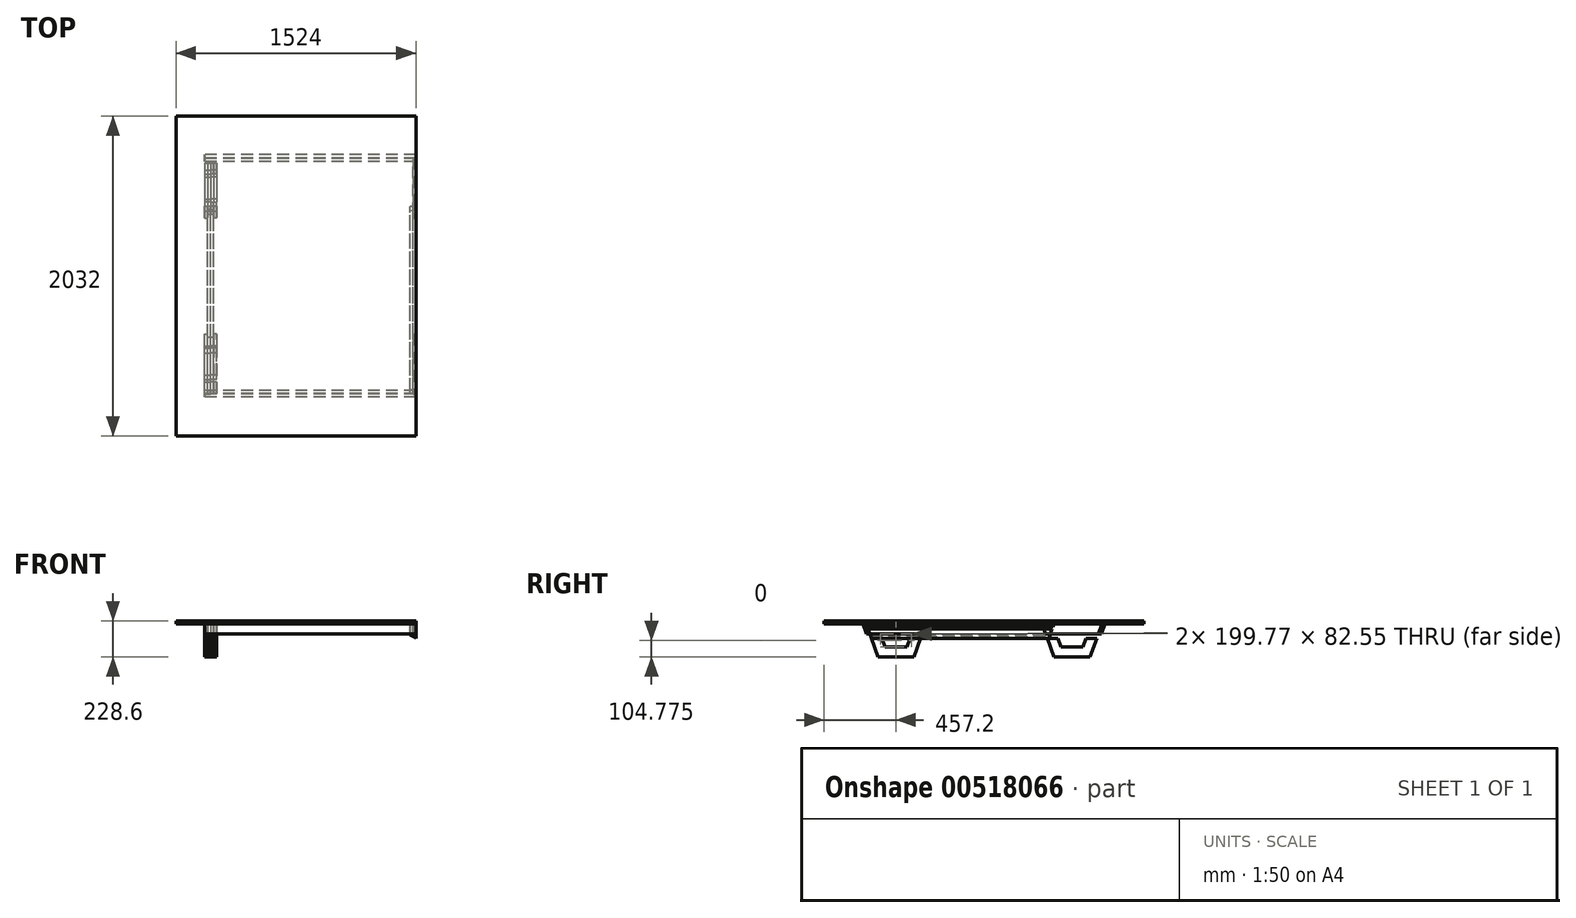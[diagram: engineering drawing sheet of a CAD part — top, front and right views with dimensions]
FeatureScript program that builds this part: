
annotation { "Feature Type Name" : "Feature", "Feature Type Description" : "" }
export const myFeature = defineFeature(function(context is Context, id is Id, definition is map)
    precondition{}
    {
        {
            var Q0;
            Q0=qCreatedBy(makeId("Top.planeOp"),FACE);
            var sketch = newSketch(context, id + "F0", { "sketchPlane" : qUnion([Q0])});
            skLineSegment(sketch, "E0.bottom", {"start": v(0, 0) * mm, "end": v(-1524, 0) * mm});
            skLineSegment(sketch, "E0.top", {"start": v(0, -2032) * mm, "end": v(-1524, -2032) * mm});
            skLineSegment(sketch, "E0.left", {"start": v(0, 0) * mm, "end": v(0, -2032) * mm});
            skLineSegment(sketch, "E0.right", {"start": v(-1524, 0) * mm, "end": v(-1524, -2032) * mm});
            skSolve(sketch);
        }
        {
            var Q0;
            Q0 = qSketchRegion(id + "F0", true);
            extrude(context, id + "F1", {"entities" : qUnion([Q0]), "depth" : 19.05 * mm, "offsetDistance" : 25.4 * mm});
        }
        {
            var Q0;
            Q0=qCreatedBy(makeId("Front.planeOp"),FACE);
            var sketch = newSketch(context, id + "F2", { "sketchPlane" : qUnion([Q0])});
            skLineSegment(sketch, "E1.bottom", {"start": v(0, -31.75) * mm, "end": v(-19.05, -31.75) * mm});
            skLineSegment(sketch, "E1.top", {"start": v(0, -69.85) * mm, "end": v(-19.05, -69.85) * mm, "construction": true});
            skLineSegment(sketch, "E1.left", {"start": v(0, -31.75) * mm, "end": v(0, -69.85) * mm});
            skLineSegment(sketch, "E1.right", {"start": v(-19.05, -31.75) * mm, "end": v(-19.05, -69.85) * mm});
            skLineSegment(sketch, "E2.bottom", {"start": v(-19.05, -69.85) * mm, "end": v(-38.1, -69.85) * mm, "construction": true});
            skLineSegment(sketch, "E2.top", {"start": v(-19.05, -6.35) * mm, "end": v(-38.1, -6.35) * mm});
            skLineSegment(sketch, "E2.left", {"start": v(-19.05, -69.85) * mm, "end": v(-19.05, -6.35) * mm});
            skLineSegment(sketch, "E2.right", {"start": v(-38.1, -69.85) * mm, "end": v(-38.1, -6.35) * mm});
            skLineSegment(sketch, "E3", {"start": v(-38.1, -69.85) * mm, "end": v(0, -91.85) * mm});
            skLineSegment(sketch, "E4", {"start": v(0, -91.85) * mm, "end": v(0, -69.85) * mm});
            skLineSegment(sketch, "E5", {"start": v(-19.05, -69.85) * mm, "end": v(-19.05, -80.85) * mm});
            skLineSegment(sketch, "E6", {"start": v(0, -91.85) * mm, "end": v(-123.42, -91.85) * mm, "construction": true});
            skSolve(sketch);
        }
        {
            var Q0;
            {var subQ0=sQuery(id+"F2.wireOp",EDGE,"E1.bottom");Q0=makeQuery(id+"F2.imprint","IMPRINT",FACE,{"disambiguationData":[TD([[makeQuery(id+"F2.imprint","IMPRINT",EDGE,{"derivedFrom":subQ0}),1.0]])]});}
            var Q1;
            Q1=makeQuery(id+"F1.opExtrude","SWEPT_FACE",FACE,{"disambiguationData":[OSD([sQuery(id+"F0.wireOp",EDGE,"E0.top")])]});
            extrude(context, id + "F3", {"entities" : qUnion([Q0]), "endBound" : BoundingType.UP_TO_SURFACE, "depth" : 25.4 * mm, "endBoundEntityFace" : qUnion([Q1]), "offsetDistance" : 25.4 * mm});
        }
        {
            var Q0;
            {var subQ3=sQuery(id+"F2.wireOp",EDGE,"E2.top");Q0=makeQuery(id+"F2.imprint","IMPRINT",FACE,{"disambiguationData":[TD([[makeQuery(id+"F2.imprint","IMPRINT",EDGE,{"derivedFrom":subQ3}),1.0]])]});}
            var Q1;
            Q1=makeQuery(id+"F3.opExtrude","CAP_FACE",FACE,{"disambiguationData":[OSD([sQuery(id+"F2.wireOp",EDGE,"E1.bottom"),sQuery(id+"F2.wireOp",EDGE,"E1.left"),sQuery(id+"F2.wireOp",EDGE,"E2.left"),sQuery(id+"F2.wireOp",EDGE,"E3"),sQuery(id+"F2.wireOp",EDGE,"E4"),sQuery(id+"F2.wireOp",EDGE,"E5")])],"isStart":false});
            extrude(context, id + "F4", {"entities" : qUnion([Q0]), "endBound" : BoundingType.UP_TO_SURFACE, "depth" : 25.4 * mm, "endBoundEntityFace" : qUnion([Q1]), "offsetDistance" : 25.4 * mm});
        }
        {
            var Q0;
            Q0=qCreatedBy(makeId("Front.planeOp"),FACE);
            var sketch = newSketch(context, id + "F5", { "sketchPlane" : qUnion([Q0])});
            skLineSegment(sketch, "E7.bottom", {"start": v(0, 0) * mm, "end": v(-19.05, 0) * mm});
            skLineSegment(sketch, "E7.top", {"start": v(0, -19.05) * mm, "end": v(-19.05, -19.05) * mm});
            skLineSegment(sketch, "E7.left", {"start": v(0, 0) * mm, "end": v(0, -19.05) * mm});
            skLineSegment(sketch, "E7.right", {"start": v(-19.05, 0) * mm, "end": v(-19.05, -19.05) * mm});
            skSolve(sketch);
        }
        {
            var Q0;
            Q0 = qSketchRegion(id + "F5", true);
            var Q1;
            Q1=makeQuery(id+"F1.opExtrude","SWEPT_FACE",FACE,{"disambiguationData":[OSD([sQuery(id+"F0.wireOp",EDGE,"E0.top")])]});
            extrude(context, id + "F6", {"entities" : qUnion([Q0]), "endBound" : BoundingType.UP_TO_SURFACE, "depth" : 25.4 * mm, "endBoundEntityFace" : qUnion([Q1]), "offsetDistance" : 25.4 * mm});
        }
        {
            var Q0;
            Q0=qCreatedBy(makeId("Front.planeOp"),FACE);
            var sketch = newSketch(context, id + "F7", { "sketchPlane" : qUnion([Q0])});
            skLineSegment(sketch, "E8.bottom", {"start": v(-1304.93, 0) * mm, "end": v(-1285.88, 0) * mm});
            skLineSegment(sketch, "E8.top", {"start": v(-1304.93, -63.5) * mm, "end": v(-1285.88, -63.5) * mm});
            skLineSegment(sketch, "E8.left", {"start": v(-1304.93, 0) * mm, "end": v(-1304.93, -63.5) * mm});
            skLineSegment(sketch, "E8.right", {"start": v(-1285.88, 0) * mm, "end": v(-1285.88, -63.5) * mm});
            skPoint(sketch, "E9", {"position": v(-1295.4, 0) * mm});
            skSolve(sketch);
        }
        {
            var Q0;
            Q0 = qSketchRegion(id + "F7", true);
            var Q1;
            Q1=makeQuery(id+"F1.opExtrude","SWEPT_FACE",FACE,{"disambiguationData":[OSD([sQuery(id+"F0.wireOp",EDGE,"E0.top")])]});
            extrude(context, id + "F8", {"entities" : qUnion([Q0]), "endBound" : BoundingType.UP_TO_SURFACE, "depth" : 25.4 * mm, "endBoundEntityFace" : qUnion([Q1]), "offsetDistance" : 25.4 * mm});
        }
        {
            var Q0;
            Q0=makeQuery(id+"F8.opExtrude","SWEPT_FACE",FACE,{"disambiguationData":[OSD([sQuery(id+"F7.wireOp",EDGE,"E8.left")])]});
            var sketch = newSketch(context, id + "F9", { "sketchPlane" : qUnion([Q0])});
            skLineSegment(sketch, "E10", {"start": v(1765.37, 0) * mm, "end": v(1689.1, -209.55) * mm});
            skLineSegment(sketch, "E11", {"start": v(1689.1, -209.55) * mm, "end": v(1460.5, -209.55) * mm});
            skLineSegment(sketch, "E12", {"start": v(1460.5, -209.55) * mm, "end": v(1384.23, 0) * mm});
            skLineSegment(sketch, "E13", {"start": v(1384.23, 0) * mm, "end": v(1765.37, 0) * mm});
            skLineSegment(sketch, "E14.0", {"start": v(1474.92, -63.5) * mm, "end": v(1674.68, -63.5) * mm});
            skLineSegment(sketch, "E14.1", {"start": v(1504.96, -146.05) * mm, "end": v(1474.92, -63.5) * mm});
            skLineSegment(sketch, "E14.2", {"start": v(1644.64, -146.05) * mm, "end": v(1504.96, -146.05) * mm});
            skLineSegment(sketch, "E14.3", {"start": v(1674.68, -63.5) * mm, "end": v(1644.64, -146.05) * mm});
            skPoint(sketch, "E15", {"position": v(1574.8, 0) * mm});
            skLineSegment(sketch, "E16", {"start": v(1016, 0) * mm, "end": v(1016, -260.73) * mm, "construction": true});
            skPoint(sketch, "E17.MirrorP", {"position": v(457.2, 0) * mm});
            skLineSegment(sketch, "E18.MirrorCS", {"start": v(357.32, -63.5) * mm, "end": v(387.36, -146.05) * mm});
            skLineSegment(sketch, "E19.MirrorCS", {"start": v(387.36, -146.05) * mm, "end": v(527.04, -146.05) * mm});
            skLineSegment(sketch, "E20.MirrorCS", {"start": v(527.04, -146.05) * mm, "end": v(557.08, -63.5) * mm});
            skLineSegment(sketch, "E21.MirrorCS", {"start": v(557.08, -63.5) * mm, "end": v(357.32, -63.5) * mm});
            skLineSegment(sketch, "E22.MirrorCS", {"start": v(266.63, 0) * mm, "end": v(342.9, -209.55) * mm});
            skLineSegment(sketch, "E23.MirrorCS", {"start": v(647.77, 0) * mm, "end": v(266.63, 0) * mm});
            skLineSegment(sketch, "E24.MirrorCS", {"start": v(342.9, -209.55) * mm, "end": v(571.5, -209.55) * mm});
            skLineSegment(sketch, "E25.MirrorCS", {"start": v(571.5, -209.55) * mm, "end": v(647.77, 0) * mm});
            skSolve(sketch);
        }
        {
            var Q0;
            Q0 = qSketchRegion(id + "F9", true);
            extrude(context, id + "F10", {"entities" : qUnion([Q0]), "depth" : 19.05 * mm, "offsetDistance" : 25.4 * mm});
        }
        {
            var Q0;
            Q0=makeQuery(id+"F10.opExtrude","CAP_FACE",FACE,{"disambiguationData":[OSD([sQuery(id+"F9.wireOp",EDGE,"E10"),sQuery(id+"F9.wireOp",EDGE,"E11"),sQuery(id+"F9.wireOp",EDGE,"E12"),sQuery(id+"F9.wireOp",EDGE,"E13"),sQuery(id+"F9.wireOp",EDGE,"E14.0"),sQuery(id+"F9.wireOp",EDGE,"E14.1"),sQuery(id+"F9.wireOp",EDGE,"E14.2"),sQuery(id+"F9.wireOp",EDGE,"E14.3")])],"isStart":true});
            var Q1;
            Q1=makeQuery(id+"F10.opExtrude","CAP_FACE",FACE,{"disambiguationData":[OSD([sQuery(id+"F9.wireOp",EDGE,"E18.MirrorCS"),sQuery(id+"F9.wireOp",EDGE,"E19.MirrorCS"),sQuery(id+"F9.wireOp",EDGE,"E20.MirrorCS"),sQuery(id+"F9.wireOp",EDGE,"E21.MirrorCS"),sQuery(id+"F9.wireOp",EDGE,"E22.MirrorCS"),sQuery(id+"F9.wireOp",EDGE,"E23.MirrorCS"),sQuery(id+"F9.wireOp",EDGE,"E24.MirrorCS"),sQuery(id+"F9.wireOp",EDGE,"E25.MirrorCS")])],"isStart":true});
            extrude(context, id + "F11", {"entities" : qUnion([Q0, Q1]), "depth" : 19.05 * mm, "offsetDistance" : 25.4 * mm});
        }
        {
            var Q0;
            Q0=makeQuery(id+"F8.opExtrude","SWEPT_BODY",BODY,{"disambiguationData":[OSD([sQuery(id+"F7.wireOp",EDGE,"E8.bottom"),sQuery(id+"F7.wireOp",EDGE,"E8.top"),sQuery(id+"F7.wireOp",EDGE,"E8.left"),sQuery(id+"F7.wireOp",EDGE,"E8.right")])]});
            var Q1;
            Q1=makeQuery(id+"F11.opExtrude","SWEPT_BODY",BODY,{"disambiguationData":[OSD([sQuery(id+"F9.wireOp",EDGE,"E10"),sQuery(id+"F9.wireOp",EDGE,"E11"),sQuery(id+"F9.wireOp",EDGE,"E12"),sQuery(id+"F9.wireOp",EDGE,"E13"),sQuery(id+"F9.wireOp",EDGE,"E14.0"),sQuery(id+"F9.wireOp",EDGE,"E14.1"),sQuery(id+"F9.wireOp",EDGE,"E14.2"),sQuery(id+"F9.wireOp",EDGE,"E14.3")])]});
            var Q2;
            Q2=makeQuery(id+"F11.opExtrude","SWEPT_BODY",BODY,{"disambiguationData":[OSD([sQuery(id+"F9.wireOp",EDGE,"E18.MirrorCS"),sQuery(id+"F9.wireOp",EDGE,"E19.MirrorCS"),sQuery(id+"F9.wireOp",EDGE,"E20.MirrorCS"),sQuery(id+"F9.wireOp",EDGE,"E21.MirrorCS"),sQuery(id+"F9.wireOp",EDGE,"E22.MirrorCS"),sQuery(id+"F9.wireOp",EDGE,"E23.MirrorCS"),sQuery(id+"F9.wireOp",EDGE,"E24.MirrorCS"),sQuery(id+"F9.wireOp",EDGE,"E25.MirrorCS")])]});
            booleanBodies(context, id + "F12", {"operationType" : BooleanOperationType.SUBTRACTION, "tools" : qUnion([Q0]), "targets" : qUnion([Q1, Q2]), "keepTools" : true});
        }
        {
            var Q0;
            Q0=makeQuery(id+"F8.opExtrude","SWEPT_FACE",FACE,{"disambiguationData":[OSD([sQuery(id+"F7.wireOp",EDGE,"E8.right")])]});
            var sketch = newSketch(context, id + "F13", { "sketchPlane" : qUnion([Q0])});
            skLineSegment(sketch, "E26.0.0", {"start": v(-1765.37, 0) * mm, "end": v(-1384.23, 0) * mm});
            skLineSegment(sketch, "E26.0.1", {"start": v(-1384.23, 0) * mm, "end": v(-1460.5, -209.55) * mm});
            skLineSegment(sketch, "E26.0.2", {"start": v(-1460.5, -209.55) * mm, "end": v(-1689.1, -209.55) * mm});
            skLineSegment(sketch, "E26.0.3", {"start": v(-1689.1, -209.55) * mm, "end": v(-1765.37, 0) * mm});
            skLineSegment(sketch, "E26.1.0", {"start": v(-342.9, -209.55) * mm, "end": v(-571.5, -209.55) * mm});
            skLineSegment(sketch, "E26.1.1", {"start": v(-571.5, -209.55) * mm, "end": v(-647.77, 0) * mm});
            skLineSegment(sketch, "E26.1.2", {"start": v(-647.77, 0) * mm, "end": v(-266.63, 0) * mm});
            skLineSegment(sketch, "E26.1.3", {"start": v(-266.63, 0) * mm, "end": v(-342.9, -209.55) * mm});
            skLineSegment(sketch, "E27.0", {"start": v(-1674.68, -63.5) * mm, "end": v(-1474.92, -63.5) * mm});
            skLineSegment(sketch, "E27.1", {"start": v(-1504.96, -146.05) * mm, "end": v(-1474.92, -63.5) * mm});
            skLineSegment(sketch, "E27.2", {"start": v(-1674.68, -63.5) * mm, "end": v(-1644.64, -146.05) * mm});
            skLineSegment(sketch, "E27.3", {"start": v(-1644.64, -146.05) * mm, "end": v(-1504.96, -146.05) * mm});
            skLineSegment(sketch, "E28.0", {"start": v(-557.08, -63.5) * mm, "end": v(-357.32, -63.5) * mm});
            skLineSegment(sketch, "E28.1", {"start": v(-357.32, -63.5) * mm, "end": v(-387.36, -146.05) * mm});
            skLineSegment(sketch, "E28.2", {"start": v(-527.04, -146.05) * mm, "end": v(-557.08, -63.5) * mm});
            skLineSegment(sketch, "E28.3", {"start": v(-387.36, -146.05) * mm, "end": v(-527.04, -146.05) * mm});
            skSolve(sketch);
        }
        {
            var Q0;
            Q0 = qSketchRegion(id + "F13", true);
            extrude(context, id + "F14", {"entities" : qUnion([Q0]), "depth" : 19.05 * mm, "offsetDistance" : 25.4 * mm});
        }
        {
            var Q0;
            Q0=makeQuery(id+"F10.opExtrude","CAP_FACE",FACE,{"disambiguationData":[OSD([sQuery(id+"F9.wireOp",EDGE,"E10"),sQuery(id+"F9.wireOp",EDGE,"E11"),sQuery(id+"F9.wireOp",EDGE,"E12"),sQuery(id+"F9.wireOp",EDGE,"E13"),sQuery(id+"F9.wireOp",EDGE,"E14.0"),sQuery(id+"F9.wireOp",EDGE,"E14.1"),sQuery(id+"F9.wireOp",EDGE,"E14.2"),sQuery(id+"F9.wireOp",EDGE,"E14.3")])],"isStart":false});
            var Q1;
            Q1=makeQuery(id+"F10.opExtrude","CAP_FACE",FACE,{"disambiguationData":[OSD([sQuery(id+"F9.wireOp",EDGE,"E18.MirrorCS"),sQuery(id+"F9.wireOp",EDGE,"E19.MirrorCS"),sQuery(id+"F9.wireOp",EDGE,"E20.MirrorCS"),sQuery(id+"F9.wireOp",EDGE,"E21.MirrorCS"),sQuery(id+"F9.wireOp",EDGE,"E22.MirrorCS"),sQuery(id+"F9.wireOp",EDGE,"E23.MirrorCS"),sQuery(id+"F9.wireOp",EDGE,"E24.MirrorCS"),sQuery(id+"F9.wireOp",EDGE,"E25.MirrorCS")])],"isStart":false});
            extrude(context, id + "F15", {"entities" : qUnion([Q0, Q1]), "depth" : 19.05 * mm, "offsetDistance" : 25.4 * mm});
        }
        {
            var Q0;
            Q0=makeQuery(id+"F8.opExtrude","SWEPT_FACE",FACE,{"disambiguationData":[OSD([sQuery(id+"F7.wireOp",EDGE,"E8.left")])]});
            var sketch = newSketch(context, id + "F16", { "sketchPlane" : qUnion([Q0])});
            skLineSegment(sketch, "E29.0", {"start": v(1765.37, 0) * mm, "end": v(1689.1, -209.55) * mm});
            skLineSegment(sketch, "E29.1", {"start": v(266.63, 0) * mm, "end": v(342.9, -209.55) * mm});
            skLineSegment(sketch, "E30", {"start": v(1765.37, 0) * mm, "end": v(2032, 0) * mm});
            skLineSegment(sketch, "E31", {"start": v(2032, 0) * mm, "end": v(2032, -209.55) * mm});
            skLineSegment(sketch, "E32", {"start": v(2032, -209.55) * mm, "end": v(1689.1, -209.55) * mm});
            skLineSegment(sketch, "E33", {"start": v(266.63, 0) * mm, "end": v(0, 0) * mm});
            skLineSegment(sketch, "E34", {"start": v(0, 0) * mm, "end": v(0, -209.55) * mm});
            skLineSegment(sketch, "E35", {"start": v(0, -209.55) * mm, "end": v(342.9, -209.55) * mm});
            skSolve(sketch);
        }
        {
            var Q0;
            Q0 = qSketchRegion(id + "F16", true);
            extrude(context, id + "F17", {"entities" : qUnion([Q0]), "operationType" : NewBodyOperationType.REMOVE, "endBound" : BoundingType.THROUGH_ALL, "oppositeDirection" : true, "depth" : 25.4 * mm, "offsetDistance" : 25.4 * mm});
        }
        {
            var Q0;
            Q0=makeQuery(id+"F8.opExtrude","SWEPT_FACE",FACE,{"disambiguationData":[OSD([sQuery(id+"F7.wireOp",EDGE,"E8.left")])]});
            extrude(context, id + "F18", {"entities" : qUnion([Q0]), "depth" : 19.05 * mm, "offsetDistance" : 25.4 * mm});
        }
        {
            var Q0;
            Q0=makeQuery(id+"F18.opExtrude","SWEPT_BODY",BODY,{"disambiguationData":[OSD([sQuery(id+"F7.wireOp",EDGE,"E8.left")])]});
            var Q1;
            Q1=makeQuery(id+"F10.opExtrude","SWEPT_BODY",BODY,{"disambiguationData":[OSD([sQuery(id+"F9.wireOp",EDGE,"E18.MirrorCS"),sQuery(id+"F9.wireOp",EDGE,"E19.MirrorCS"),sQuery(id+"F9.wireOp",EDGE,"E20.MirrorCS"),sQuery(id+"F9.wireOp",EDGE,"E21.MirrorCS"),sQuery(id+"F9.wireOp",EDGE,"E22.MirrorCS"),sQuery(id+"F9.wireOp",EDGE,"E23.MirrorCS"),sQuery(id+"F9.wireOp",EDGE,"E24.MirrorCS"),sQuery(id+"F9.wireOp",EDGE,"E25.MirrorCS")])]});
            var Q2;
            Q2=makeQuery(id+"F10.opExtrude","SWEPT_BODY",BODY,{"disambiguationData":[OSD([sQuery(id+"F9.wireOp",EDGE,"E10"),sQuery(id+"F9.wireOp",EDGE,"E11"),sQuery(id+"F9.wireOp",EDGE,"E12"),sQuery(id+"F9.wireOp",EDGE,"E13"),sQuery(id+"F9.wireOp",EDGE,"E14.0"),sQuery(id+"F9.wireOp",EDGE,"E14.1"),sQuery(id+"F9.wireOp",EDGE,"E14.2"),sQuery(id+"F9.wireOp",EDGE,"E14.3")])]});
            booleanBodies(context, id + "F19", {"operationType" : BooleanOperationType.SUBTRACTION, "tools" : qUnion([Q0]), "targets" : qUnion([Q1, Q2]), "keepTools" : true});
        }
        {
            var Q0;
            Q0=makeQuery(id+"F15.opExtrude","CAP_FACE",FACE,{"disambiguationData":[OSD([sQuery(id+"F9.wireOp",EDGE,"E10"),sQuery(id+"F9.wireOp",EDGE,"E11"),sQuery(id+"F9.wireOp",EDGE,"E12"),sQuery(id+"F9.wireOp",EDGE,"E13"),sQuery(id+"F9.wireOp",EDGE,"E14.0"),sQuery(id+"F9.wireOp",EDGE,"E14.1"),sQuery(id+"F9.wireOp",EDGE,"E14.2"),sQuery(id+"F9.wireOp",EDGE,"E14.3")])],"isStart":false});
            var sketch = newSketch(context, id + "F20", { "sketchPlane" : qUnion([Q0])});
            skLineSegment(sketch, "E36", {"start": v(1765.37, 0) * mm, "end": v(1785.64, 0) * mm});
            skLineSegment(sketch, "E37", {"start": v(1785.64, 0) * mm, "end": v(1762.53, -63.5) * mm});
            skLineSegment(sketch, "E38", {"start": v(1762.53, -63.5) * mm, "end": v(1742.26, -63.5) * mm});
            skLineSegment(sketch, "E39", {"start": v(1742.26, -63.5) * mm, "end": v(1765.37, 0) * mm});
            skLineSegment(sketch, "E40", {"start": v(1016, 0) * mm, "end": v(1016, 513.07) * mm, "construction": true});
            skLineSegment(sketch, "E41.MirrorCS", {"start": v(269.47, -63.5) * mm, "end": v(289.74, -63.5) * mm});
            skLineSegment(sketch, "E42.MirrorCS", {"start": v(266.63, 0) * mm, "end": v(246.36, 0) * mm});
            skLineSegment(sketch, "E43.MirrorCS", {"start": v(289.74, -63.5) * mm, "end": v(266.63, 0) * mm});
            skLineSegment(sketch, "E44.MirrorCS", {"start": v(246.36, 0) * mm, "end": v(269.47, -63.5) * mm});
            skLineSegment(sketch, "E45", {"start": v(1574.8, 0) * mm, "end": v(1574.8, 198.43) * mm, "construction": true});
            skLineSegment(sketch, "E46.MirrorCS", {"start": v(1387.07, -63.5) * mm, "end": v(1407.34, -63.5) * mm});
            skLineSegment(sketch, "E47.MirrorCS", {"start": v(1384.23, 0) * mm, "end": v(1363.96, 0) * mm});
            skLineSegment(sketch, "E48.MirrorCS", {"start": v(1407.34, -63.5) * mm, "end": v(1384.23, 0) * mm});
            skLineSegment(sketch, "E49.MirrorCS", {"start": v(1363.96, 0) * mm, "end": v(1387.07, -63.5) * mm});
            skLineSegment(sketch, "E50.MirrorCS", {"start": v(624.66, -63.5) * mm, "end": v(647.77, 0) * mm});
            skLineSegment(sketch, "E51.MirrorCS", {"start": v(668.04, 0) * mm, "end": v(644.93, -63.5) * mm});
            skLineSegment(sketch, "E52.MirrorCS", {"start": v(644.93, -63.5) * mm, "end": v(624.66, -63.5) * mm});
            skLineSegment(sketch, "E53.MirrorCS", {"start": v(647.77, 0) * mm, "end": v(668.04, 0) * mm});
            skSolve(sketch);
        }
        {
            var Q0;
            Q0 = qSketchRegion(id + "F20", true);
            var Q1;
            Q1=makeQuery(id+"F3.opExtrude","SWEPT_FACE",FACE,{"disambiguationData":[OSD([sQuery(id+"F2.wireOp",EDGE,"E1.left"),sQuery(id+"F2.wireOp",EDGE,"E4")])]});
            extrude(context, id + "F21", {"entities" : qUnion([Q0]), "endBound" : BoundingType.UP_TO_SURFACE, "oppositeDirection" : true, "depth" : 25.4 * mm, "endBoundEntityFace" : qUnion([Q1]), "offsetDistance" : 25.4 * mm});
        }
        {
            var Q0;
            Q0=makeQuery(id+"F3.opExtrude","SWEPT_FACE",FACE,{"disambiguationData":[OSD([sQuery(id+"F2.wireOp",EDGE,"E1.left"),sQuery(id+"F2.wireOp",EDGE,"E4")])]});
            var sketch = newSketch(context, id + "F22", { "sketchPlane" : qUnion([Q0])});
            skLineSegment(sketch, "E54", {"start": v(-300.06, -91.85) * mm, "end": v(-266.63, 0) * mm});
            skLineSegment(sketch, "E55", {"start": v(-266.63, 0) * mm, "end": v(-571.43, 0) * mm});
            skLineSegment(sketch, "E56", {"start": v(-571.43, 0) * mm, "end": v(-604.86, -91.85) * mm});
            skLineSegment(sketch, "E57", {"start": v(-604.86, -91.85) * mm, "end": v(-300.06, -91.85) * mm});
            skSolve(sketch);
        }
        {
            var Q0;
            Q0 = qSketchRegion(id + "F22", true);
            extrude(context, id + "F23", {"entities" : qUnion([Q0]), "operationType" : NewBodyOperationType.REMOVE, "endBound" : BoundingType.THROUGH_ALL, "oppositeDirection" : true, "depth" : 25.4 * mm, "offsetDistance" : 25.4 * mm});
        }
        {
            var Q0;
            Q0=makeQuery(id+"F18.opExtrude","SWEPT_BODY",BODY,{"disambiguationData":[OSD([sQuery(id+"F7.wireOp",EDGE,"E8.left")])]});
            var Q1;
            Q1=makeQuery(id+"F8.opExtrude","SWEPT_BODY",BODY,{"disambiguationData":[OSD([sQuery(id+"F7.wireOp",EDGE,"E8.bottom"),sQuery(id+"F7.wireOp",EDGE,"E8.top"),sQuery(id+"F7.wireOp",EDGE,"E8.left"),sQuery(id+"F7.wireOp",EDGE,"E8.right")])]});
            var Q2;
            Q2=makeQuery(id+"F21.opExtrude","SWEPT_BODY",BODY,{"disambiguationData":[OSD([sQuery(id+"F20.wireOp",EDGE,"E50.MirrorCS"),sQuery(id+"F20.wireOp",EDGE,"E51.MirrorCS"),sQuery(id+"F20.wireOp",EDGE,"E52.MirrorCS"),sQuery(id+"F20.wireOp",EDGE,"E53.MirrorCS")])]});
            var Q3;
            Q3=makeQuery(id+"F21.opExtrude","SWEPT_BODY",BODY,{"disambiguationData":[OSD([sQuery(id+"F20.wireOp",EDGE,"E46.MirrorCS"),sQuery(id+"F20.wireOp",EDGE,"E47.MirrorCS"),sQuery(id+"F20.wireOp",EDGE,"E48.MirrorCS"),sQuery(id+"F20.wireOp",EDGE,"E49.MirrorCS")])]});
            booleanBodies(context, id + "F24", {"operationType" : BooleanOperationType.SUBTRACTION, "tools" : qUnion([Q0, Q1]), "targets" : qUnion([Q2, Q3]), "keepTools" : true});
        }
        {
            var Q0;
            Q0=makeQuery(id+"F24.opBoolean","SPLIT",BODY,{"disambiguationData":[OD(0.0)],"derivedFrom":makeQuery(id+"F21.opExtrude","SWEPT_BODY",BODY,{"disambiguationData":[OSD([sQuery(id+"F20.wireOp",EDGE,"E50.MirrorCS"),sQuery(id+"F20.wireOp",EDGE,"E51.MirrorCS"),sQuery(id+"F20.wireOp",EDGE,"E52.MirrorCS"),sQuery(id+"F20.wireOp",EDGE,"E53.MirrorCS")])]})});
            var Q1;
            Q1=makeQuery(id+"F24.opBoolean","SPLIT",BODY,{"disambiguationData":[OD(0.0)],"derivedFrom":makeQuery(id+"F21.opExtrude","SWEPT_BODY",BODY,{"disambiguationData":[OSD([sQuery(id+"F20.wireOp",EDGE,"E46.MirrorCS"),sQuery(id+"F20.wireOp",EDGE,"E47.MirrorCS"),sQuery(id+"F20.wireOp",EDGE,"E48.MirrorCS"),sQuery(id+"F20.wireOp",EDGE,"E49.MirrorCS")])]})});
            deleteBodies(context, id + "F25", {"entities" : qUnion([Q0, Q1])});
        }
        {
            var Q0;
            Q0=makeQuery(id+"F1.opExtrude","SWEPT_FACE",FACE,{"disambiguationData":[OSD([sQuery(id+"F0.wireOp",EDGE,"E0.left")])]});
            var sketch = newSketch(context, id + "F26", { "sketchPlane" : qUnion([Q0])});
            skLineSegment(sketch, "E58.0", {"start": v(-1742.26, -63.5) * mm, "end": v(-1765.37, 0) * mm});
            skLineSegment(sketch, "E58.1", {"start": v(-1384.23, 0) * mm, "end": v(-1407.34, -63.5) * mm});
            skLineSegment(sketch, "E58.2", {"start": v(-647.77, 0) * mm, "end": v(-624.66, -63.5) * mm});
            skLineSegment(sketch, "E58.3", {"start": v(-266.63, 0) * mm, "end": v(-289.74, -63.5) * mm});
            skLineSegment(sketch, "E58.4", {"start": v(-266.63, 0) * mm, "end": v(-647.77, 0) * mm});
            skLineSegment(sketch, "E59", {"start": v(-1742.26, -63.5) * mm, "end": v(-1407.34, -63.5) * mm});
            skLineSegment(sketch, "E60", {"start": v(-624.66, -63.5) * mm, "end": v(-289.74, -63.5) * mm});
            skPoint(sketch, "E61.orphan", {"position": v(-2032, 0) * mm});
            skLineSegment(sketch, "E62.trimOffspring", {"start": v(-1384.23, 0) * mm, "end": v(-1765.37, 0) * mm});
            skPoint(sketch, "E63.orphan", {"position": v(0, 0) * mm});
            skSolve(sketch);
        }
        {
            var Q0;
            Q0 = qSketchRegion(id + "F26", true);
            extrude(context, id + "F27", {"entities" : qUnion([Q0]), "oppositeDirection" : true, "depth" : 19.05 * mm, "offsetDistance" : 25.4 * mm});
        }
    });
